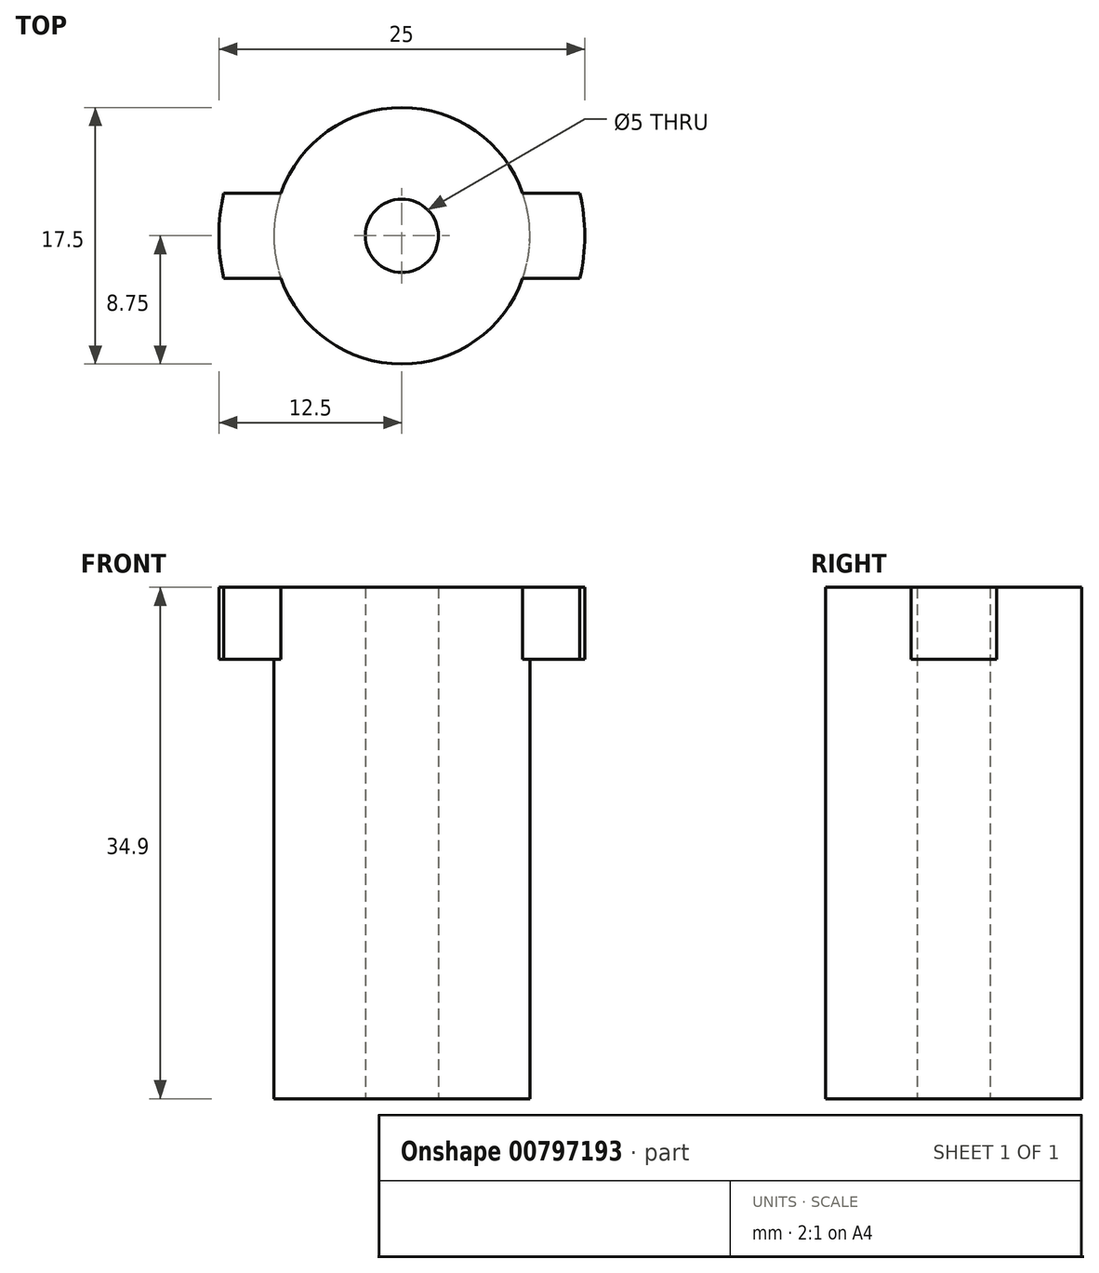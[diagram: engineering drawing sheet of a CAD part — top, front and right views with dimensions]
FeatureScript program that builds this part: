
annotation { "Feature Type Name" : "Feature", "Feature Type Description" : "" }
export const myFeature = defineFeature(function(context is Context, id is Id, definition is map)
    precondition{}
    {
        {
            var Q0;
            Q0=qCreatedBy(makeId("Top.planeOp"),FACE);
            var sketch = newSketch(context, id + "F0", { "sketchPlane" : qUnion([Q0])});
            skCircle(sketch, "E0", {"center": v(0, 0) * mm, "radius": 8.75 * mm});
            skSolve(sketch);
        }
        {
            var Q0;
            Q0 = qSketchRegion(id + "F0", true);
            extrude(context, id + "F1", {"entities" : qUnion([Q0]), "depth" : 30 * mm, "offsetDistance" : 25 * mm});
        }
        {
            var Q0;
            Q0=makeQuery(id+"F1.opExtrude","CAP_FACE",FACE,{"disambiguationData":[OSD([sQuery(id+"F0.wireOp",EDGE,"E0")])],"isStart":false});
            var sketch = newSketch(context, id + "F2", { "sketchPlane" : qUnion([Q0])});
            skArc(sketch, "E1", {"start": v(-8.25, 2.92) * mm, "mid": v(0, 8.75) * mm, "end": v(8.25, 2.92) * mm});
            skArc(sketch, "E2", {"start": v(-8.25, -2.92) * mm, "mid": v(0, -8.75) * mm, "end": v(8.25, -2.92) * mm});
            skLineSegment(sketch, "E3", {"start": v(-8.25, 2.92) * mm, "end": v(-12.15, 2.92) * mm});
            skLineSegment(sketch, "E4", {"start": v(-8.25, -2.92) * mm, "end": v(-12.15, -2.92) * mm});
            skLineSegment(sketch, "E5", {"start": v(12.15, 2.92) * mm, "end": v(8.25, 2.92) * mm});
            skLineSegment(sketch, "E6", {"start": v(12.15, -2.92) * mm, "end": v(8.25, -2.92) * mm});
            skArc(sketch, "E7", {"start": v(-12.15, 2.92) * mm, "mid": v(-12.5, 0) * mm, "end": v(-12.15, -2.92) * mm});
            skArc(sketch, "E8", {"start": v(12.15, 2.92) * mm, "mid": v(12.5, 0) * mm, "end": v(12.15, -2.92) * mm});
            skSolve(sketch);
        }
        {
            var Q0;
            Q0 = qSketchRegion(id + "F2", true);
            extrude(context, id + "F3", {"entities" : qUnion([Q0]), "operationType" : NewBodyOperationType.ADD, "depth" : (5 - 0.1) * mm, "offsetDistance" : 25 * mm});
        }
        {
            var Q0;
            Q0=makeQuery(id+"F1.opExtrude","CAP_FACE",FACE,{"disambiguationData":[OSD([sQuery(id+"F0.wireOp",EDGE,"E0")])],"isStart":true});
            var sketch = newSketch(context, id + "F4", { "sketchPlane" : qUnion([Q0])});
            skPoint(sketch, "E9", {"position": v(0, 0) * mm});
            skSolve(sketch);
        }
        {
            var Q0;
            Q0=sQuery(id+"F4.wireOp",VERTEX,"E9");
            var Q1;
            Q1=makeQuery(id+"F1.opExtrude","SWEPT_BODY",BODY,{"disambiguationData":[OSD([sQuery(id+"F0.wireOp",EDGE,"E0")])]});
            hole(context, id + "F5", {"style" : HoleStyle.SIMPLE, "endStyle" : HoleEndStyle.THROUGH, "holeDiameter" : 5 * mm, "majorDiameter" : 5 * mm, "isTappedThrough" : true, "tappedDepth" : 12 * mm, "tapClearance" : 3, "locations" : qUnion([Q0]), "scope" : qUnion([Q1])});
        }
    });
